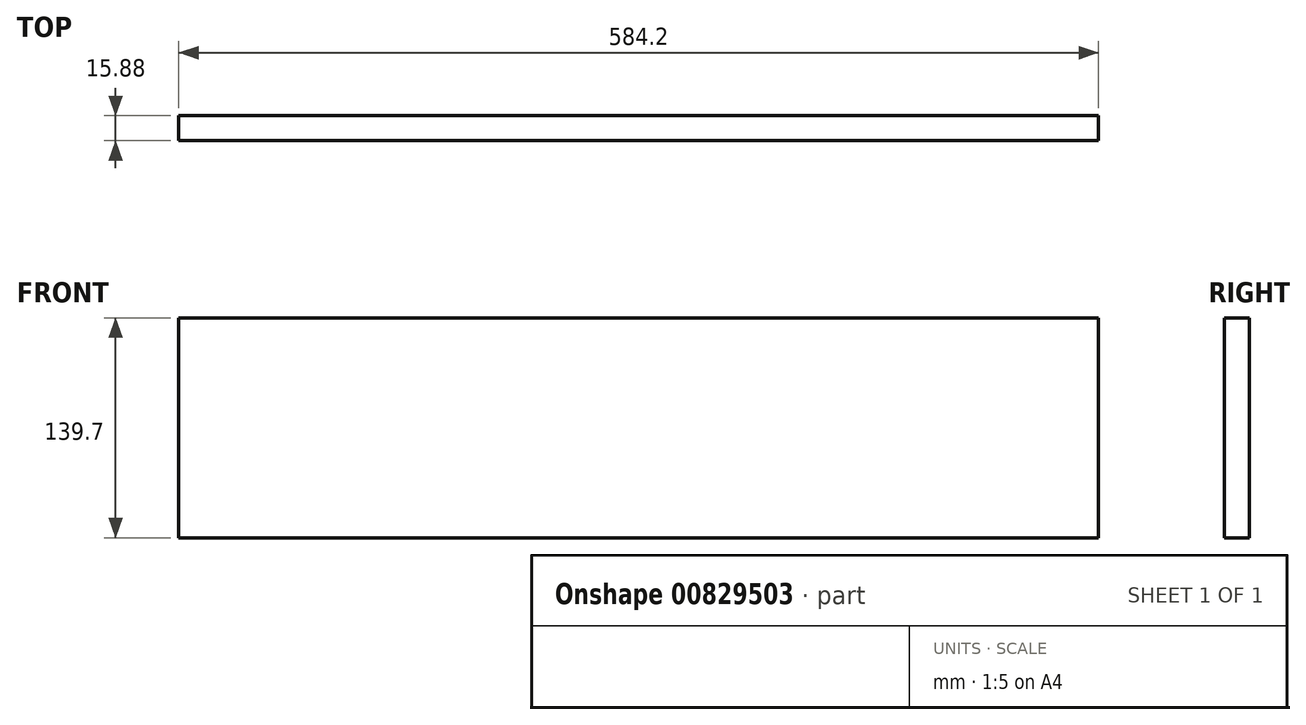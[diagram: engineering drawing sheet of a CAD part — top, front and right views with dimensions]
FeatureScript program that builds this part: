
annotation { "Feature Type Name" : "Feature", "Feature Type Description" : "" }
export const myFeature = defineFeature(function(context is Context, id is Id, definition is map)
    precondition{}
    {
        {
            var Q0;
            Q0=qCreatedBy(makeId("Right.planeOp"),FACE);
            var sketch = newSketch(context, id + "F0", { "sketchPlane" : qUnion([Q0])});
            skLineSegment(sketch, "E0.bottom", {"start": v(0, 0) * mm, "end": v(15.88, 0) * mm});
            skLineSegment(sketch, "E0.top", {"start": v(0, 139.7) * mm, "end": v(15.87, 139.7) * mm});
            skLineSegment(sketch, "E0.left", {"start": v(0, 0) * mm, "end": v(0, 139.7) * mm});
            skLineSegment(sketch, "E0.right", {"start": v(15.88, 0) * mm, "end": v(15.88, 139.7) * mm});
            skSolve(sketch);
        }
        {
            var Q0;
            Q0=makeQuery(id+"F0.imprint","IMPRINT",FACE,{"disambiguationData":[TD([[makeQuery(id+"F0.imprint","IMPRINT",EDGE,{"derivedFrom":sQuery(id+"F0.wireOp",EDGE,"E0.bottom")}),1.0]])]});
            extrude(context, id + "F1", {"entities" : qUnion([Q0]), "depth" : 584.2 * mm, "offsetDistance" : 25.4 * mm});
        }
    });
